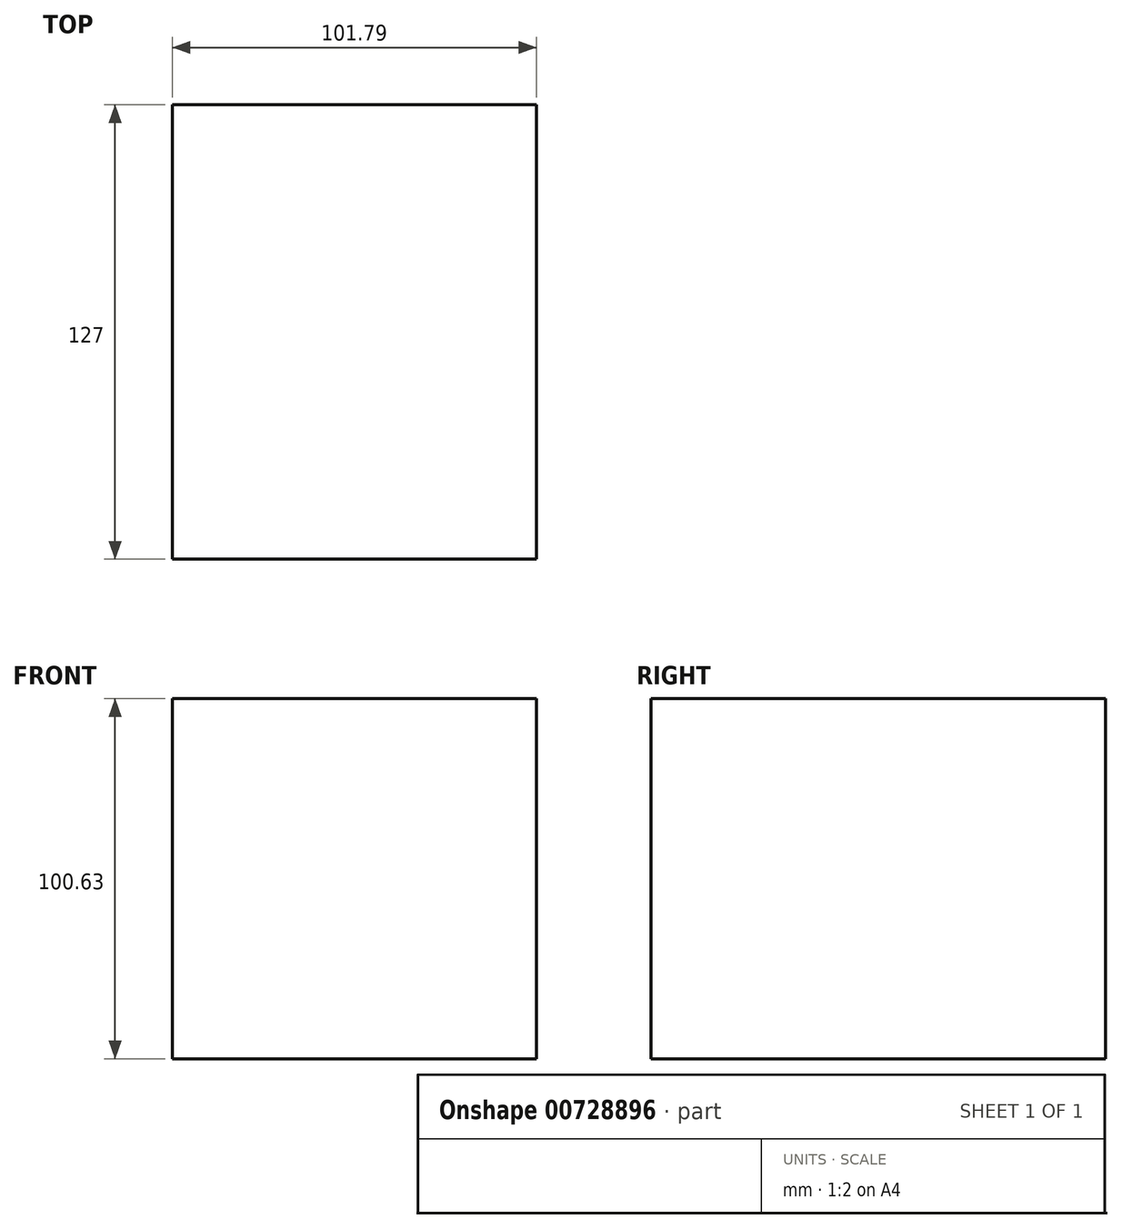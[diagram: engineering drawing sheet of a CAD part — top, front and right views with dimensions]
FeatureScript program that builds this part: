
annotation { "Feature Type Name" : "Feature", "Feature Type Description" : "" }
export const myFeature = defineFeature(function(context is Context, id is Id, definition is map)
    precondition{}
    {
        {
            var Q0;
            Q0=qCreatedBy(makeId("Front.planeOp"),FACE);
            var sketch = newSketch(context, id + "F0", { "sketchPlane" : qUnion([Q0])});
            skLineSegment(sketch, "E0.bottom", {"start": v(-56.7, 57.46) * mm, "end": v(45.1, 57.46) * mm});
            skLineSegment(sketch, "E0.top", {"start": v(-56.7, -43.17) * mm, "end": v(45.1, -43.17) * mm});
            skLineSegment(sketch, "E0.left", {"start": v(-56.7, 57.46) * mm, "end": v(-56.7, -43.17) * mm});
            skLineSegment(sketch, "E0.right", {"start": v(45.1, 57.46) * mm, "end": v(45.1, -43.17) * mm});
            skSolve(sketch);
        }
        {
            var Q0;
            Q0=makeQuery(id+"F0.imprint","IMPRINT",FACE,{"disambiguationData":[TD([[makeQuery(id+"F0.imprint","IMPRINT",EDGE,{"derivedFrom":sQuery(id+"F0.wireOp",EDGE,"E0.bottom")}),-1.0]])]});
            extrude(context, id + "F1", {"entities" : qUnion([Q0]), "depth" : 127 * mm, "offsetDistance" : 25.4 * mm});
        }
    });
